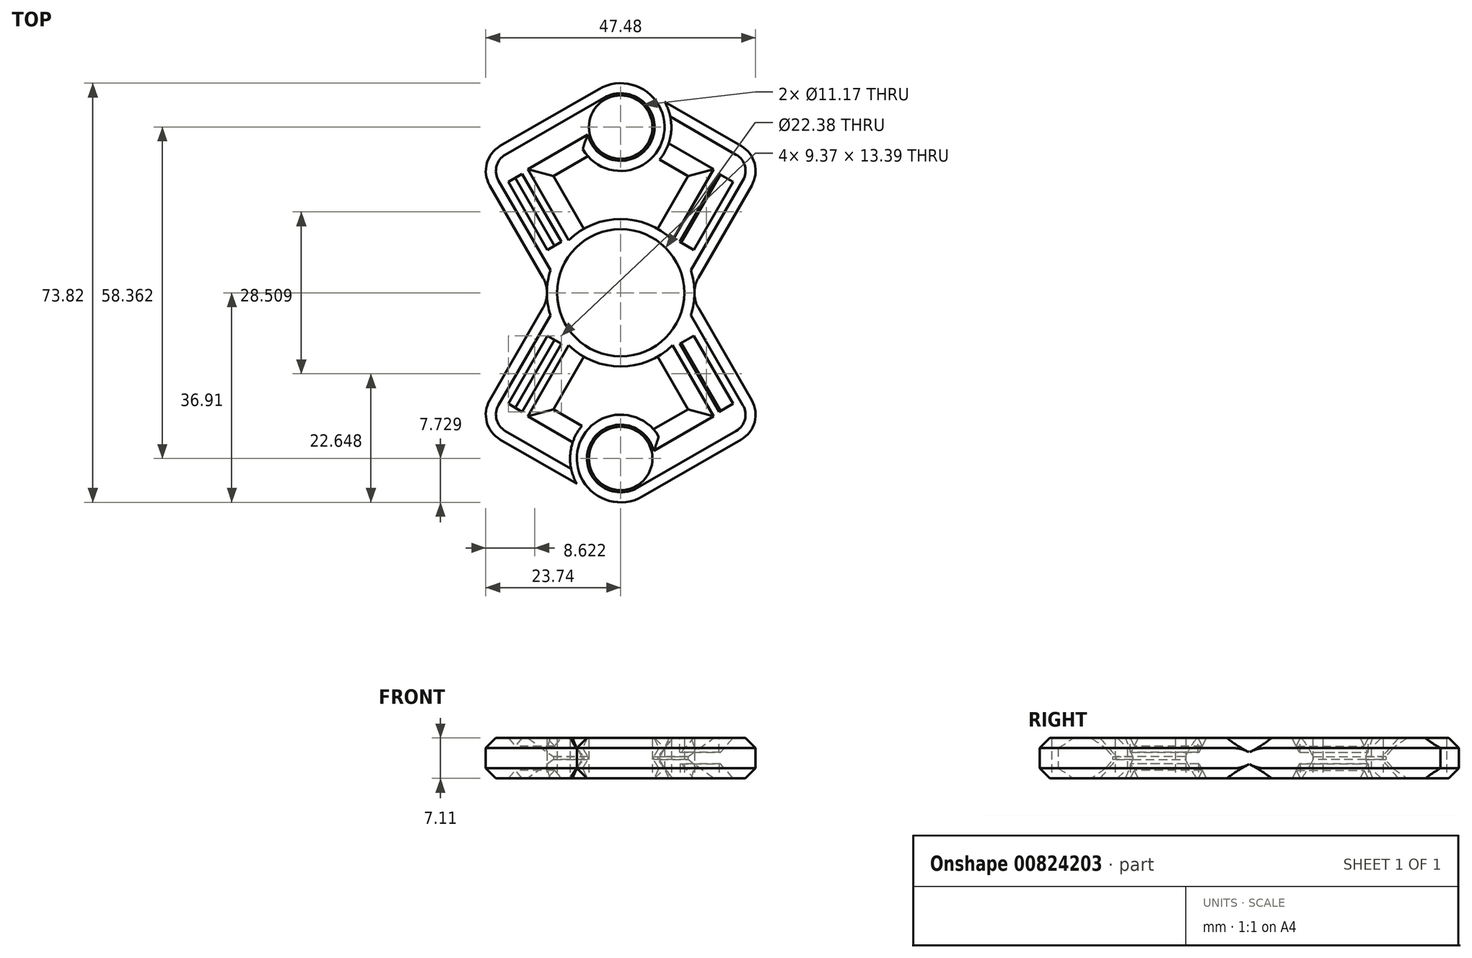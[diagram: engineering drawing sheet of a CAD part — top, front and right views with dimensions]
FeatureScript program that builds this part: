
annotation { "Feature Type Name" : "Feature", "Feature Type Description" : "" }
export const myFeature = defineFeature(function(context is Context, id is Id, definition is map)
    precondition{}
    {
        {
            var Q0;
            Q0=qCreatedBy(makeId("Top.planeOp"),FACE);
            var sketch = newSketch(context, id + "F0", { "sketchPlane" : qUnion([Q0])});
            skCircle(sketch, "E0", {"center": v(0, 0) * mm, "radius": 11.19 * mm});
            skCircle(sketch, "E1", {"center": v(0, 0) * mm, "radius": 12.99 * mm});
            skCircle(sketch, "E2.cCircle", {"center": v(0, 0) * mm, "radius": 33 * mm, "construction": true});
            skLineSegment(sketch, "E2.0", {"start": v(0, -38.1) * mm, "end": v(-33, -19.05) * mm});
            skLineSegment(sketch, "E2.1", {"start": v(-33, -19.05) * mm, "end": v(-33, 19.05) * mm});
            skLineSegment(sketch, "E2.2", {"start": v(-33, 19.05) * mm, "end": v(0, 38.1) * mm});
            skLineSegment(sketch, "E2.3", {"start": v(0, 38.1) * mm, "end": v(33, 19.05) * mm});
            skLineSegment(sketch, "E2.4", {"start": v(33, 19.05) * mm, "end": v(33, -19.05) * mm});
            skLineSegment(sketch, "E2.5", {"start": v(33, -19.05) * mm, "end": v(0, -38.1) * mm});
            skPoint(sketch, "E2.0.midPoint", {"position": v(-16.5, -28.58) * mm});
            skLineSegment(sketch, "E3", {"start": v(16.5, 28.57) * mm, "end": v(-16.5, -28.58) * mm});
            skLineSegment(sketch, "E4", {"start": v(-16.5, 28.57) * mm, "end": v(16.5, -28.57) * mm});
            skLineSegment(sketch, "E5", {"start": v(25.6, 23.32) * mm, "end": v(12.92, 1.34) * mm});
            skLineSegment(sketch, "E6.MirrorCS", {"start": v(-25.6, 23.32) * mm, "end": v(-12.92, 1.34) * mm});
            skLineSegment(sketch, "E7.MirrorCS", {"start": v(25.6, -23.32) * mm, "end": v(12.92, -1.34) * mm});
            skLineSegment(sketch, "E8.MirrorCS", {"start": v(-25.6, -23.32) * mm, "end": v(-12.92, -1.34) * mm});
            skLineSegment(sketch, "E9", {"start": v(-11.86, 20.54) * mm, "end": v(0, 27.38) * mm});
            skLineSegment(sketch, "E10.MirrorCS", {"start": v(11.86, 20.54) * mm, "end": v(0, 27.38) * mm});
            skLineSegment(sketch, "E11.MirrorCS", {"start": v(11.86, -20.54) * mm, "end": v(0, -27.38) * mm});
            skLineSegment(sketch, "E12.MirrorCS", {"start": v(-11.86, -20.54) * mm, "end": v(0, -27.38) * mm});
            skCircle(sketch, "E13", {"center": v(0, 29.18) * mm, "radius": 5.59 * mm});
            skCircle(sketch, "E14.MirrorC", {"center": v(0, -29.18) * mm, "radius": 5.59 * mm});
            skCircle(sketch, "E15", {"center": v(0, 29.18) * mm, "radius": 7.72 * mm});
            skCircle(sketch, "E16.MirrorC", {"center": v(0, -29.18) * mm, "radius": 7.72 * mm});
            skCircle(sketch, "E17", {"center": v(0, 29.18) * mm, "radius": 8.92 * mm});
            skCircle(sketch, "E18.MirrorC", {"center": v(0, -29.18) * mm, "radius": 8.92 * mm});
            skSolve(sketch);
        }
        {
            var Q0;
            {var subQ6=sQuery(id+"F0.wireOp",EDGE,"E7.MirrorCS");Q0=makeQuery(id+"F0.imprint","IMPRINT",FACE,{"disambiguationData":[TD([[makeQuery(id+"F0.imprint","IMPRINT",EDGE,{"derivedFrom":subQ6}),1.0]])]});}
            var Q1;
            {var subQ6=sQuery(id+"F0.wireOp",EDGE,"E8.MirrorCS");Q1=makeQuery(id+"F0.imprint","IMPRINT",FACE,{"disambiguationData":[TD([[makeQuery(id+"F0.imprint","IMPRINT",EDGE,{"derivedFrom":subQ6}),-1.0]])]});}
            var Q2;
            {var subQ4=sQuery(id+"F0.wireOp",EDGE,"E6.MirrorCS");Q2=makeQuery(id+"F0.imprint","IMPRINT",FACE,{"disambiguationData":[TD([[makeQuery(id+"F0.imprint","IMPRINT",EDGE,{"derivedFrom":subQ4}),1.0]])]});}
            var Q3;
            {var subQ0=sQuery(id+"F0.wireOp",EDGE,"E4");var subQ1=sQuery(id+"F0.wireOp",EDGE,"E2.2");var subQ2=makeQuery(id+"F0.imprint","INTERSECT",VERTEX,{"derivedFrom":[subQ1,subQ0]});Q3=makeQuery(id+"F0.imprint","IMPRINT",FACE,{"disambiguationData":[TD([[makeQuery(id+"F0.imprint","IMPRINT",EDGE,{"disambiguationData":[TD([[subQ2,-1.0]])],"derivedFrom":subQ1}),-1.0]])]});}
            var Q4;
            {var subQ1=sQuery(id+"F0.wireOp",EDGE,"E9");var subQ5=sQuery(id+"F0.wireOp",EDGE,"E15");var subQ9=makeQuery(id+"F0.imprint","INTERSECT",VERTEX,{"derivedFrom":[subQ1,subQ5]});Q4=makeQuery(id+"F0.imprint","IMPRINT",FACE,{"disambiguationData":[TD([[makeQuery(id+"F0.imprint","IMPRINT",EDGE,{"disambiguationData":[TD([[subQ9,-1.0]])],"derivedFrom":subQ1}),1.0]])]});}
            var Q5;
            {var subQ0=sQuery(id+"F0.wireOp",EDGE,"E15");var subQ1=sQuery(id+"F0.wireOp",EDGE,"E9");var subQ2=makeQuery(id+"F0.imprint","INTERSECT",VERTEX,{"derivedFrom":[subQ1,subQ0]});Q5=makeQuery(id+"F0.imprint","IMPRINT",FACE,{"disambiguationData":[TD([[makeQuery(id+"F0.imprint","IMPRINT",EDGE,{"disambiguationData":[TD([[subQ2,-1.0]])],"derivedFrom":subQ1}),-1.0]])]});}
            var Q6;
            {var subQ0=sQuery(id+"F0.wireOp",EDGE,"E16.MirrorC");var subQ4=sQuery(id+"F0.wireOp",EDGE,"E11.MirrorCS");var subQ9=makeQuery(id+"F0.imprint","INTERSECT",VERTEX,{"derivedFrom":[subQ4,subQ0]});Q6=makeQuery(id+"F0.imprint","IMPRINT",FACE,{"disambiguationData":[TD([[makeQuery(id+"F0.imprint","IMPRINT",EDGE,{"disambiguationData":[TD([[subQ9,-1.0]])],"derivedFrom":subQ4}),1.0]])]});}
            var Q7;
            {var subQ0=sQuery(id+"F0.wireOp",EDGE,"E16.MirrorC");var subQ1=sQuery(id+"F0.wireOp",EDGE,"E11.MirrorCS");var subQ2=makeQuery(id+"F0.imprint","INTERSECT",VERTEX,{"derivedFrom":[subQ1,subQ0]});Q7=makeQuery(id+"F0.imprint","IMPRINT",FACE,{"disambiguationData":[TD([[makeQuery(id+"F0.imprint","IMPRINT",EDGE,{"disambiguationData":[TD([[subQ2,-1.0]])],"derivedFrom":subQ1}),-1.0]])]});}
            var Q8;
            {var subQ0=sQuery(id+"F0.wireOp",EDGE,"E4");var subQ1=sQuery(id+"F0.wireOp",EDGE,"E2.5");var subQ2=makeQuery(id+"F0.imprint","INTERSECT",VERTEX,{"derivedFrom":[subQ1,subQ0]});Q8=makeQuery(id+"F0.imprint","IMPRINT",FACE,{"disambiguationData":[TD([[makeQuery(id+"F0.imprint","IMPRINT",EDGE,{"disambiguationData":[TD([[subQ2,-1.0]])],"derivedFrom":subQ1}),-1.0]])]});}
            var Q9;
            {var subQ0=sQuery(id+"F0.wireOp",EDGE,"E18.MirrorC");var subQ1=sQuery(id+"F0.wireOp",EDGE,"E2.5");var subQ2=makeQuery(id+"F0.imprint","INTERSECT",VERTEX,{"derivedFrom":[subQ1,subQ0]});Q9=makeQuery(id+"F0.imprint","IMPRINT",FACE,{"disambiguationData":[TD([[makeQuery(id+"F0.imprint","IMPRINT",EDGE,{"disambiguationData":[TD([[subQ2,-1.0]])],"derivedFrom":subQ1}),-1.0]])]});}
            var Q10;
            {var subQ0=sQuery(id+"F0.wireOp",EDGE,"E3");var subQ1=sQuery(id+"F0.wireOp",EDGE,"E2.0");var subQ2=makeQuery(id+"F0.imprint","INTERSECT",VERTEX,{"derivedFrom":[subQ1,subQ0]});Q10=makeQuery(id+"F0.imprint","IMPRINT",FACE,{"disambiguationData":[TD([[makeQuery(id+"F0.imprint","IMPRINT",EDGE,{"disambiguationData":[TD([[subQ2,1.0]])],"derivedFrom":subQ1}),-1.0]])]});}
            var Q11;
            {var subQ0=sQuery(id+"F0.wireOp",EDGE,"E17");var subQ1=sQuery(id+"F0.wireOp",EDGE,"E2.2");var subQ2=makeQuery(id+"F0.imprint","INTERSECT",VERTEX,{"derivedFrom":[subQ1,subQ0]});Q11=makeQuery(id+"F0.imprint","IMPRINT",FACE,{"disambiguationData":[TD([[makeQuery(id+"F0.imprint","IMPRINT",EDGE,{"disambiguationData":[TD([[subQ2,-1.0]])],"derivedFrom":subQ1}),-1.0]])]});}
            var Q12;
            {var subQ0=sQuery(id+"F0.wireOp",EDGE,"E3");var subQ1=sQuery(id+"F0.wireOp",EDGE,"E2.3");var subQ2=makeQuery(id+"F0.imprint","INTERSECT",VERTEX,{"derivedFrom":[subQ1,subQ0]});Q12=makeQuery(id+"F0.imprint","IMPRINT",FACE,{"disambiguationData":[TD([[makeQuery(id+"F0.imprint","IMPRINT",EDGE,{"disambiguationData":[TD([[subQ2,1.0]])],"derivedFrom":subQ1}),-1.0]])]});}
            var Q13;
            {var subQ6=sQuery(id+"F0.wireOp",EDGE,"E5");Q13=makeQuery(id+"F0.imprint","IMPRINT",FACE,{"disambiguationData":[TD([[makeQuery(id+"F0.imprint","IMPRINT",EDGE,{"derivedFrom":subQ6}),-1.0]])]});}
            extrude(context, id + "F1", {"entities" : qUnion([Q0, Q1, Q2, Q3, Q4, Q5, Q6, Q7, Q8, Q9, Q10, Q11, Q12, Q13]), "depth" : 7.11 * mm, "offsetDistance" : 25.4 * mm});
        }
        {
            var Q0;
            {var subQ0=sQuery(id+"F0.wireOp",EDGE,"E3");var subQ1=sQuery(id+"F0.wireOp",EDGE,"E0");var subQ2=makeQuery(id+"F0.imprint","INTERSECT",VERTEX,{"disambiguationData":[OD(1.0)],"derivedFrom":[subQ1,subQ0]});Q0=makeQuery(id+"F0.imprint","IMPRINT",FACE,{"disambiguationData":[TD([[makeQuery(id+"F0.imprint","IMPRINT",EDGE,{"disambiguationData":[TD([[subQ2,-1.0]])],"derivedFrom":subQ1}),-1.0]])]});}
            var Q1;
            {var subQ5=sQuery(id+"F0.wireOp",EDGE,"E4");var subQ7=sQuery(id+"F0.wireOp",EDGE,"E0");var subQ9=makeQuery(id+"F0.imprint","INTERSECT",VERTEX,{"disambiguationData":[OD(0.0)],"derivedFrom":[subQ7,subQ5]});Q1=makeQuery(id+"F0.imprint","IMPRINT",FACE,{"disambiguationData":[TD([[makeQuery(id+"F0.imprint","IMPRINT",EDGE,{"disambiguationData":[TD([[subQ9,-1.0]])],"derivedFrom":subQ7}),-1.0]])]});}
            var Q2;
            {var subQ0=sQuery(id+"F0.wireOp",EDGE,"E4");var subQ1=sQuery(id+"F0.wireOp",EDGE,"E0");var subQ2=makeQuery(id+"F0.imprint","INTERSECT",VERTEX,{"disambiguationData":[OD(0.0)],"derivedFrom":[subQ1,subQ0]});Q2=makeQuery(id+"F0.imprint","IMPRINT",FACE,{"disambiguationData":[TD([[makeQuery(id+"F0.imprint","IMPRINT",EDGE,{"disambiguationData":[TD([[subQ2,1.0]])],"derivedFrom":subQ1}),-1.0]])]});}
            var Q3;
            {var subQ5=sQuery(id+"F0.wireOp",EDGE,"E3");var subQ7=sQuery(id+"F0.wireOp",EDGE,"E0");var subQ8=makeQuery(id+"F0.imprint","INTERSECT",VERTEX,{"disambiguationData":[OD(0.0)],"derivedFrom":[subQ7,subQ5]});Q3=makeQuery(id+"F0.imprint","IMPRINT",FACE,{"disambiguationData":[TD([[makeQuery(id+"F0.imprint","IMPRINT",EDGE,{"disambiguationData":[TD([[subQ8,1.0]])],"derivedFrom":subQ7}),-1.0]])]});}
            extrude(context, id + "F2", {"entities" : qUnion([Q0, Q1, Q2, Q3]), "depth" : 7.11 * mm, "offsetDistance" : 25.4 * mm});
        }
        {
            var Q0;
            Q0=makeQuery(id+"F1.opExtrude","SWEPT_EDGE",EDGE,{"disambiguationData":[OSD([sQuery(id+"F0.wireOp",EDGE,"E2.5"),sQuery(id+"F0.wireOp",EDGE,"E7.MirrorCS")])]});
            var Q1;
            Q1=makeQuery(id+"F1.opExtrude","SWEPT_EDGE",EDGE,{"disambiguationData":[OSD([sQuery(id+"F0.wireOp",EDGE,"E2.3"),sQuery(id+"F0.wireOp",EDGE,"E5")])]});
            var Q2;
            Q2=makeQuery(id+"F1.opExtrude","SWEPT_EDGE",EDGE,{"disambiguationData":[OSD([sQuery(id+"F0.wireOp",EDGE,"E2.2"),sQuery(id+"F0.wireOp",EDGE,"E6.MirrorCS")])]});
            var Q3;
            Q3=makeQuery(id+"F1.opExtrude","SWEPT_EDGE",EDGE,{"disambiguationData":[OSD([sQuery(id+"F0.wireOp",EDGE,"E2.0"),sQuery(id+"F0.wireOp",EDGE,"E8.MirrorCS")])]});
            fillet(context, id + "F3", {"entities" : qUnion([Q0, Q1, Q2, Q3]), "radius" : 5.08 * mm, "tangentPropagation" : true, "allowEdgeOverflow" : false});
        }
        {
            var Q0;
            Q0=makeQuery(id+"F1.opExtrude","CAP_EDGE",EDGE,{"disambiguationData":[OSD([sQuery(id+"F0.wireOp",EDGE,"E7.MirrorCS")])],"isStart":true});
            var Q1;
            Q1=makeQuery(id+"F1.opExtrude","CAP_EDGE",EDGE,{"disambiguationData":[OSD([sQuery(id+"F0.wireOp",EDGE,"E2.5")])],"isStart":true});
            var Q2;
            Q2=makeQuery(id+"F1.opExtrude","CAP_EDGE",EDGE,{"disambiguationData":[OSD([sQuery(id+"F0.wireOp",EDGE,"E5")])],"isStart":true});
            var Q3;
            {var subQ0=sQuery(id+"F0.wireOp",EDGE,"E2.3");var subQ1=makeQuery(id+"F0.imprint","INTERSECT",VERTEX,{"derivedFrom":[subQ0,sQuery(id+"F0.wireOp",EDGE,"E3")]});Q3=makeQuery(id+"F1.opExtrude","CAP_EDGE",EDGE,{"disambiguationData":[OSD([subQ0]),TDD([makeQuery(id+"F0.imprint","IMPRINT",EDGE,{"disambiguationData":[TD([[subQ1,1.0]])],"derivedFrom":subQ0}),makeQuery(id+"F0.imprint","IMPRINT",EDGE,{"disambiguationData":[TD([[subQ1,-1.0]])],"derivedFrom":subQ0})])],"isStart":true});}
            var Q4;
            Q4=makeQuery(id+"F1.opExtrude","CAP_EDGE",EDGE,{"disambiguationData":[OSD([sQuery(id+"F0.wireOp",EDGE,"E2.2")])],"isStart":true});
            var Q5;
            Q5=makeQuery(id+"F1.opExtrude","CAP_EDGE",EDGE,{"disambiguationData":[OSD([sQuery(id+"F0.wireOp",EDGE,"E6.MirrorCS")])],"isStart":true});
            var Q6;
            Q6=makeQuery(id+"F1.opExtrude","CAP_EDGE",EDGE,{"disambiguationData":[OSD([sQuery(id+"F0.wireOp",EDGE,"E8.MirrorCS")])],"isStart":true});
            var Q7;
            {var subQ0=sQuery(id+"F0.wireOp",EDGE,"E2.0");var subQ1=makeQuery(id+"F0.imprint","INTERSECT",VERTEX,{"derivedFrom":[subQ0,sQuery(id+"F0.wireOp",EDGE,"E3")]});Q7=makeQuery(id+"F1.opExtrude","CAP_EDGE",EDGE,{"disambiguationData":[OSD([subQ0]),TDD([makeQuery(id+"F0.imprint","IMPRINT",EDGE,{"disambiguationData":[TD([[subQ1,1.0]])],"derivedFrom":subQ0}),makeQuery(id+"F0.imprint","IMPRINT",EDGE,{"disambiguationData":[TD([[subQ1,-1.0]])],"derivedFrom":subQ0})])],"isStart":true});}
            var Q8;
            Q8=makeQuery(id+"F1.opExtrude","CAP_EDGE",EDGE,{"disambiguationData":[OSD([sQuery(id+"F0.wireOp",EDGE,"E16.MirrorC")])],"isStart":true});
            var Q9;
            Q9=makeQuery(id+"F1.opExtrude","CAP_EDGE",EDGE,{"disambiguationData":[OSD([sQuery(id+"F0.wireOp",EDGE,"E15")])],"isStart":true});
            var Q10;
            Q10=makeQuery(id+"F1.opExtrude","CAP_EDGE",EDGE,{"disambiguationData":[OSD([sQuery(id+"F0.wireOp",EDGE,"E15")])],"isStart":false});
            var Q11;
            Q11=makeQuery(id+"F1.opExtrude","CAP_EDGE",EDGE,{"disambiguationData":[OSD([sQuery(id+"F0.wireOp",EDGE,"E2.2")])],"isStart":false});
            var Q12;
            Q12=makeQuery(id+"F1.opExtrude","CAP_EDGE",EDGE,{"disambiguationData":[OSD([sQuery(id+"F0.wireOp",EDGE,"E6.MirrorCS")])],"isStart":false});
            var Q13;
            Q13=makeQuery(id+"F1.opExtrude","CAP_EDGE",EDGE,{"disambiguationData":[OSD([sQuery(id+"F0.wireOp",EDGE,"E8.MirrorCS")])],"isStart":false});
            var Q14;
            {var subQ0=sQuery(id+"F0.wireOp",EDGE,"E2.0");var subQ1=makeQuery(id+"F0.imprint","INTERSECT",VERTEX,{"derivedFrom":[subQ0,sQuery(id+"F0.wireOp",EDGE,"E3")]});Q14=makeQuery(id+"F1.opExtrude","CAP_EDGE",EDGE,{"disambiguationData":[OSD([subQ0]),TDD([makeQuery(id+"F0.imprint","IMPRINT",EDGE,{"disambiguationData":[TD([[subQ1,1.0]])],"derivedFrom":subQ0}),makeQuery(id+"F0.imprint","IMPRINT",EDGE,{"disambiguationData":[TD([[subQ1,-1.0]])],"derivedFrom":subQ0})])],"isStart":false});}
            var Q15;
            Q15=makeQuery(id+"F1.opExtrude","CAP_EDGE",EDGE,{"disambiguationData":[OSD([sQuery(id+"F0.wireOp",EDGE,"E16.MirrorC")])],"isStart":false});
            var Q16;
            Q16=makeQuery(id+"F1.opExtrude","CAP_EDGE",EDGE,{"disambiguationData":[OSD([sQuery(id+"F0.wireOp",EDGE,"E2.5")])],"isStart":false});
            var Q17;
            Q17=makeQuery(id+"F1.opExtrude","CAP_EDGE",EDGE,{"disambiguationData":[OSD([sQuery(id+"F0.wireOp",EDGE,"E7.MirrorCS")])],"isStart":false});
            var Q18;
            Q18=makeQuery(id+"F1.opExtrude","CAP_EDGE",EDGE,{"disambiguationData":[OSD([sQuery(id+"F0.wireOp",EDGE,"E5")])],"isStart":false});
            var Q19;
            {var subQ0=sQuery(id+"F0.wireOp",EDGE,"E2.3");var subQ1=makeQuery(id+"F0.imprint","INTERSECT",VERTEX,{"derivedFrom":[subQ0,sQuery(id+"F0.wireOp",EDGE,"E3")]});Q19=makeQuery(id+"F1.opExtrude","CAP_EDGE",EDGE,{"disambiguationData":[OSD([subQ0]),TDD([makeQuery(id+"F0.imprint","IMPRINT",EDGE,{"disambiguationData":[TD([[subQ1,1.0]])],"derivedFrom":subQ0}),makeQuery(id+"F0.imprint","IMPRINT",EDGE,{"disambiguationData":[TD([[subQ1,-1.0]])],"derivedFrom":subQ0})])],"isStart":false});}
            chamfer(context, id + "F4", {"entities" : qUnion([Q0, Q1, Q2, Q3, Q4, Q5, Q6, Q7, Q8, Q9, Q10, Q11, Q12, Q13, Q14, Q15, Q16, Q17, Q18, Q19]), "width" : 1.78 * mm, "tangentPropagation" : true});
        }
        {
            var Q0;
            Q0=makeQuery(id+"F1.opExtrude","CAP_EDGE",EDGE,{"disambiguationData":[OSD([sQuery(id+"F0.wireOp",EDGE,"E11.MirrorCS")])],"isStart":true});
            var Q1;
            {var subQ0=sQuery(id+"F0.wireOp",EDGE,"E4");Q1=makeQuery(id+"F1.opExtrude","CAP_EDGE",EDGE,{"disambiguationData":[OSD([subQ0]),TDD([makeQuery(id+"F0.imprint","IMPRINT",EDGE,{"disambiguationData":[TD([[makeQuery(id+"F0.imprint","INTERSECT",VERTEX,{"derivedFrom":[subQ0,sQuery(id+"F0.wireOp",EDGE,"E11.MirrorCS")]}),1.0]])],"derivedFrom":subQ0})])],"isStart":true});}
            var Q2;
            Q2=makeQuery(id+"F1.opExtrude","CAP_EDGE",EDGE,{"disambiguationData":[OSD([sQuery(id+"F0.wireOp",EDGE,"E12.MirrorCS")])],"isStart":true});
            var Q3;
            {var subQ0=sQuery(id+"F0.wireOp",EDGE,"E3");Q3=makeQuery(id+"F1.opExtrude","CAP_EDGE",EDGE,{"disambiguationData":[OSD([subQ0]),TDD([makeQuery(id+"F0.imprint","IMPRINT",EDGE,{"disambiguationData":[TD([[makeQuery(id+"F0.imprint","INTERSECT",VERTEX,{"derivedFrom":[subQ0,sQuery(id+"F0.wireOp",EDGE,"E12.MirrorCS")]}),1.0]])],"derivedFrom":subQ0})])],"isStart":true});}
            var Q4;
            {var subQ0=sQuery(id+"F0.wireOp",EDGE,"E4");Q4=makeQuery(id+"F1.opExtrude","CAP_EDGE",EDGE,{"disambiguationData":[OSD([subQ0]),TDD([makeQuery(id+"F0.imprint","IMPRINT",EDGE,{"disambiguationData":[TD([[makeQuery(id+"F0.imprint","INTERSECT",VERTEX,{"derivedFrom":[subQ0,sQuery(id+"F0.wireOp",EDGE,"E11.MirrorCS")]}),1.0]])],"derivedFrom":subQ0})])],"isStart":false});}
            var Q5;
            Q5=makeQuery(id+"F1.opExtrude","CAP_EDGE",EDGE,{"disambiguationData":[OSD([sQuery(id+"F0.wireOp",EDGE,"E11.MirrorCS")])],"isStart":false});
            var Q6;
            Q6=makeQuery(id+"F1.opExtrude","CAP_EDGE",EDGE,{"disambiguationData":[OSD([sQuery(id+"F0.wireOp",EDGE,"E12.MirrorCS")])],"isStart":false});
            var Q7;
            {var subQ0=sQuery(id+"F0.wireOp",EDGE,"E3");Q7=makeQuery(id+"F1.opExtrude","CAP_EDGE",EDGE,{"disambiguationData":[OSD([subQ0]),TDD([makeQuery(id+"F0.imprint","IMPRINT",EDGE,{"disambiguationData":[TD([[makeQuery(id+"F0.imprint","INTERSECT",VERTEX,{"derivedFrom":[subQ0,sQuery(id+"F0.wireOp",EDGE,"E12.MirrorCS")]}),1.0]])],"derivedFrom":subQ0})])],"isStart":false});}
            var Q8;
            {var subQ0=sQuery(id+"F0.wireOp",EDGE,"E4");Q8=makeQuery(id+"F1.opExtrude","CAP_EDGE",EDGE,{"disambiguationData":[OSD([subQ0]),TDD([makeQuery(id+"F0.imprint","IMPRINT",EDGE,{"disambiguationData":[TD([[makeQuery(id+"F0.imprint","INTERSECT",VERTEX,{"derivedFrom":[subQ0,sQuery(id+"F0.wireOp",EDGE,"E9")]}),-1.0]])],"derivedFrom":subQ0})])],"isStart":true});}
            var Q9;
            Q9=makeQuery(id+"F1.opExtrude","CAP_EDGE",EDGE,{"disambiguationData":[OSD([sQuery(id+"F0.wireOp",EDGE,"E9")])],"isStart":true});
            var Q10;
            {var subQ0=sQuery(id+"F0.wireOp",EDGE,"E3");Q10=makeQuery(id+"F1.opExtrude","CAP_EDGE",EDGE,{"disambiguationData":[OSD([subQ0]),TDD([makeQuery(id+"F0.imprint","IMPRINT",EDGE,{"disambiguationData":[TD([[makeQuery(id+"F0.imprint","INTERSECT",VERTEX,{"derivedFrom":[subQ0,sQuery(id+"F0.wireOp",EDGE,"E10.MirrorCS")]}),-1.0]])],"derivedFrom":subQ0})])],"isStart":true});}
            var Q11;
            Q11=makeQuery(id+"F1.opExtrude","CAP_EDGE",EDGE,{"disambiguationData":[OSD([sQuery(id+"F0.wireOp",EDGE,"E10.MirrorCS")])],"isStart":true});
            var Q12;
            {var subQ0=sQuery(id+"F0.wireOp",EDGE,"E3");Q12=makeQuery(id+"F1.opExtrude","CAP_EDGE",EDGE,{"disambiguationData":[OSD([subQ0]),TDD([makeQuery(id+"F0.imprint","IMPRINT",EDGE,{"disambiguationData":[TD([[makeQuery(id+"F0.imprint","INTERSECT",VERTEX,{"derivedFrom":[subQ0,sQuery(id+"F0.wireOp",EDGE,"E10.MirrorCS")]}),-1.0]])],"derivedFrom":subQ0})])],"isStart":false});}
            var Q13;
            Q13=makeQuery(id+"F1.opExtrude","CAP_EDGE",EDGE,{"disambiguationData":[OSD([sQuery(id+"F0.wireOp",EDGE,"E10.MirrorCS")])],"isStart":false});
            var Q14;
            {var subQ0=sQuery(id+"F0.wireOp",EDGE,"E4");Q14=makeQuery(id+"F1.opExtrude","CAP_EDGE",EDGE,{"disambiguationData":[OSD([subQ0]),TDD([makeQuery(id+"F0.imprint","IMPRINT",EDGE,{"disambiguationData":[TD([[makeQuery(id+"F0.imprint","INTERSECT",VERTEX,{"derivedFrom":[subQ0,sQuery(id+"F0.wireOp",EDGE,"E9")]}),-1.0]])],"derivedFrom":subQ0})])],"isStart":false});}
            var Q15;
            Q15=makeQuery(id+"F1.opExtrude","CAP_EDGE",EDGE,{"disambiguationData":[OSD([sQuery(id+"F0.wireOp",EDGE,"E9")])],"isStart":false});
            chamfer(context, id + "F5", {"entities" : qUnion([Q0, Q1, Q2, Q3, Q4, Q5, Q6, Q7, Q8, Q9, Q10, Q11, Q12, Q13, Q14, Q15]), "width" : 3.3 * mm, "tangentPropagation" : true});
        }
        {
            var Q0;
            Q0=makeQuery(id+"F1.opExtrude","SWEPT_BODY",BODY,{"disambiguationData":[OSD([sQuery(id+"F0.wireOp",EDGE,"E1"),sQuery(id+"F0.wireOp",EDGE,"E2.3"),sQuery(id+"F0.wireOp",EDGE,"E3"),sQuery(id+"F0.wireOp",EDGE,"E5"),sQuery(id+"F0.wireOp",EDGE,"E10.MirrorCS"),sQuery(id+"F0.wireOp",EDGE,"E17")])]});
            var Q1;
            Q1=makeQuery(id+"F1.opExtrude","SWEPT_BODY",BODY,{"disambiguationData":[OSD([sQuery(id+"F0.wireOp",EDGE,"E1"),sQuery(id+"F0.wireOp",EDGE,"E2.2"),sQuery(id+"F0.wireOp",EDGE,"E4"),sQuery(id+"F0.wireOp",EDGE,"E6.MirrorCS"),sQuery(id+"F0.wireOp",EDGE,"E9"),sQuery(id+"F0.wireOp",EDGE,"E13"),sQuery(id+"F0.wireOp",EDGE,"E15")])]});
            var Q2;
            Q2=makeQuery(id+"F1.opExtrude","SWEPT_BODY",BODY,{"disambiguationData":[OSD([sQuery(id+"F0.wireOp",EDGE,"E1"),sQuery(id+"F0.wireOp",EDGE,"E2.0"),sQuery(id+"F0.wireOp",EDGE,"E3"),sQuery(id+"F0.wireOp",EDGE,"E8.MirrorCS"),sQuery(id+"F0.wireOp",EDGE,"E12.MirrorCS"),sQuery(id+"F0.wireOp",EDGE,"E18.MirrorC")])]});
            var Q3;
            Q3=makeQuery(id+"F1.opExtrude","SWEPT_BODY",BODY,{"disambiguationData":[OSD([sQuery(id+"F0.wireOp",EDGE,"E1"),sQuery(id+"F0.wireOp",EDGE,"E2.5"),sQuery(id+"F0.wireOp",EDGE,"E4"),sQuery(id+"F0.wireOp",EDGE,"E7.MirrorCS"),sQuery(id+"F0.wireOp",EDGE,"E11.MirrorCS"),sQuery(id+"F0.wireOp",EDGE,"E14.MirrorC"),sQuery(id+"F0.wireOp",EDGE,"E16.MirrorC")])]});
            var Q4;
            Q4=makeQuery(id+"F2.opExtrude","SWEPT_BODY",BODY,{"disambiguationData":[OSD([sQuery(id+"F0.wireOp",EDGE,"E0"),sQuery(id+"F0.wireOp",EDGE,"E1")])]});
            booleanBodies(context, id + "F6", {"operationType" : BooleanOperationType.UNION, "tools" : qUnion([Q0, Q1, Q2, Q3, Q4])});
        }
        {
            var Q0;
            Q0=makeQuery(id+"F1.opExtrude","SWEPT_EDGE",EDGE,{"disambiguationData":[OSD([sQuery(id+"F0.wireOp",EDGE,"E1"),sQuery(id+"F0.wireOp",EDGE,"E8.MirrorCS")])]});
            var Q1;
            Q1=makeQuery(id+"F1.opExtrude","SWEPT_EDGE",EDGE,{"disambiguationData":[OSD([sQuery(id+"F0.wireOp",EDGE,"E1"),sQuery(id+"F0.wireOp",EDGE,"E6.MirrorCS")])]});
            var Q2;
            Q2=makeQuery(id+"F1.opExtrude","SWEPT_EDGE",EDGE,{"disambiguationData":[OSD([sQuery(id+"F0.wireOp",EDGE,"E1"),sQuery(id+"F0.wireOp",EDGE,"E7.MirrorCS")])]});
            var Q3;
            Q3=makeQuery(id+"F1.opExtrude","SWEPT_EDGE",EDGE,{"disambiguationData":[OSD([sQuery(id+"F0.wireOp",EDGE,"E1"),sQuery(id+"F0.wireOp",EDGE,"E5")])]});
            fillet(context, id + "F7", {"entities" : qUnion([Q0, Q1, Q2, Q3]), "radius" : 5.08 * mm, "tangentPropagation" : true, "allowEdgeOverflow" : false});
        }
        {
            var Q0;
            {var subQ0=sQuery(id+"F0.wireOp",EDGE,"E4");var subQ1=sQuery(id+"F0.wireOp",EDGE,"E1");var subQ2=sQuery(id+"F0.wireOp",EDGE,"E3");Q0=makeQuery(id+"F6.opBoolean","MERGE",FACE,{"derivedFrom":[makeQuery(id+"F2.opExtrude","CAP_FACE",FACE,{"disambiguationData":[OSD([sQuery(id+"F0.wireOp",EDGE,"E0"),subQ1])],"isStart":true}),makeQuery(id+"F1.opExtrude","CAP_FACE",FACE,{"disambiguationData":[OSD([subQ1,sQuery(id+"F0.wireOp",EDGE,"E2.3"),subQ2,sQuery(id+"F0.wireOp",EDGE,"E5"),sQuery(id+"F0.wireOp",EDGE,"E10.MirrorCS"),sQuery(id+"F0.wireOp",EDGE,"E17")])],"isStart":true}),makeQuery(id+"F1.opExtrude","CAP_FACE",FACE,{"disambiguationData":[OSD([subQ1,sQuery(id+"F0.wireOp",EDGE,"E2.2"),subQ0,sQuery(id+"F0.wireOp",EDGE,"E6.MirrorCS"),sQuery(id+"F0.wireOp",EDGE,"E9"),sQuery(id+"F0.wireOp",EDGE,"E13"),sQuery(id+"F0.wireOp",EDGE,"E15")])],"isStart":true}),makeQuery(id+"F1.opExtrude","CAP_FACE",FACE,{"disambiguationData":[OSD([subQ1,sQuery(id+"F0.wireOp",EDGE,"E2.0"),subQ2,sQuery(id+"F0.wireOp",EDGE,"E8.MirrorCS"),sQuery(id+"F0.wireOp",EDGE,"E12.MirrorCS"),sQuery(id+"F0.wireOp",EDGE,"E18.MirrorC")])],"isStart":true}),makeQuery(id+"F1.opExtrude","CAP_FACE",FACE,{"disambiguationData":[OSD([subQ1,sQuery(id+"F0.wireOp",EDGE,"E2.5"),subQ0,sQuery(id+"F0.wireOp",EDGE,"E7.MirrorCS"),sQuery(id+"F0.wireOp",EDGE,"E11.MirrorCS"),sQuery(id+"F0.wireOp",EDGE,"E14.MirrorC"),sQuery(id+"F0.wireOp",EDGE,"E16.MirrorC")])],"isStart":true})]});}
            var sketch = newSketch(context, id + "F8", { "sketchPlane" : qUnion([Q0])});
            skLineSegment(sketch, "E19", {"start": v(10.43, 8.97) * mm, "end": v(17.34, 20.95) * mm});
            skLineSegment(sketch, "E20", {"start": v(17.34, 20.95) * mm, "end": v(19.8, 19.53) * mm});
            skLineSegment(sketch, "E21.MirrorCS", {"start": v(10.43, 8.97) * mm, "end": v(12.88, 7.56) * mm});
            skLineSegment(sketch, "E22.MirrorCS", {"start": v(17.34, 20.95) * mm, "end": v(10.43, 8.97) * mm});
            skLineSegment(sketch, "E23.MirrorCS", {"start": v(19.8, 19.53) * mm, "end": v(12.88, 7.56) * mm});
            skLineSegment(sketch, "E24.MirrorCS", {"start": v(-17.34, 20.95) * mm, "end": v(-19.8, 19.53) * mm});
            skLineSegment(sketch, "E25.MirrorCS", {"start": v(-19.8, 19.53) * mm, "end": v(-12.88, 7.56) * mm});
            skLineSegment(sketch, "E26.MirrorCS", {"start": v(-10.43, 8.97) * mm, "end": v(-12.88, 7.56) * mm});
            skLineSegment(sketch, "E27.MirrorCS", {"start": v(-17.34, 20.95) * mm, "end": v(-10.43, 8.97) * mm});
            skLineSegment(sketch, "E28.MirrorCS", {"start": v(-17.34, -20.95) * mm, "end": v(-19.8, -19.53) * mm});
            skLineSegment(sketch, "E29.MirrorCS", {"start": v(17.34, -20.95) * mm, "end": v(19.8, -19.53) * mm});
            skLineSegment(sketch, "E30.MirrorCS", {"start": v(10.43, -8.97) * mm, "end": v(12.88, -7.56) * mm});
            skLineSegment(sketch, "E31.MirrorCS", {"start": v(-10.43, -8.97) * mm, "end": v(-12.88, -7.56) * mm});
            skLineSegment(sketch, "E32.MirrorCS", {"start": v(10.43, -8.97) * mm, "end": v(17.34, -20.95) * mm});
            skLineSegment(sketch, "E33.MirrorCS", {"start": v(-19.8, -19.53) * mm, "end": v(-12.88, -7.56) * mm});
            skLineSegment(sketch, "E34.MirrorCS", {"start": v(-17.34, -20.95) * mm, "end": v(-10.43, -8.97) * mm});
            skLineSegment(sketch, "E35.MirrorCS", {"start": v(17.34, -20.95) * mm, "end": v(10.43, -8.97) * mm});
            skLineSegment(sketch, "E36.MirrorCS", {"start": v(19.8, -19.53) * mm, "end": v(12.88, -7.56) * mm});
            skSolve(sketch);
        }
        {
            var Q0;
            Q0=makeQuery(id+"F8.imprint","IMPRINT",FACE,{"disambiguationData":[TD([[makeQuery(id+"F8.imprint","IMPRINT",EDGE,{"derivedFrom":sQuery(id+"F8.wireOp",EDGE,"E24.MirrorCS")}),1.0]])]});
            var Q1;
            Q1=makeQuery(id+"F8.imprint","IMPRINT",FACE,{"disambiguationData":[TD([[makeQuery(id+"F8.imprint","IMPRINT",EDGE,{"derivedFrom":sQuery(id+"F8.wireOp",EDGE,"E28.MirrorCS")}),-1.0]])]});
            var Q2;
            Q2=makeQuery(id+"F8.imprint","IMPRINT",FACE,{"disambiguationData":[TD([[makeQuery(id+"F8.imprint","IMPRINT",EDGE,{"derivedFrom":sQuery(id+"F8.wireOp",EDGE,"E29.MirrorCS")}),1.0]])]});
            var Q3;
            Q3=makeQuery(id+"F8.imprint","IMPRINT",FACE,{"disambiguationData":[TD([[makeQuery(id+"F8.imprint","IMPRINT",EDGE,{"derivedFrom":sQuery(id+"F8.wireOp",EDGE,"E20")}),-1.0]])]});
            extrude(context, id + "F9", {"entities" : qUnion([Q0, Q1, Q2, Q3]), "operationType" : NewBodyOperationType.REMOVE, "oppositeDirection" : true, "depth" : 2.54 * mm, "offsetDistance" : 25.4 * mm});
        }
        {
            var Q0;
            Q0=makeQuery(id+"F9.boolean.opBoolean","COPY",EDGE,{"derivedFrom":makeQuery(id+"F9.opExtrude","CAP_EDGE",EDGE,{"disambiguationData":[OSD([sQuery(id+"F8.wireOp",EDGE,"E23.MirrorCS")])],"isStart":false})});
            var Q1;
            Q1=makeQuery(id+"F9.boolean.opBoolean","COPY",EDGE,{"derivedFrom":makeQuery(id+"F9.opExtrude","CAP_EDGE",EDGE,{"disambiguationData":[OSD([sQuery(id+"F8.wireOp",EDGE,"E22.MirrorCS")])],"isStart":false})});
            var Q2;
            Q2=makeQuery(id+"F9.boolean.opBoolean","COPY",EDGE,{"derivedFrom":makeQuery(id+"F9.opExtrude","CAP_EDGE",EDGE,{"disambiguationData":[OSD([sQuery(id+"F8.wireOp",EDGE,"E27.MirrorCS")])],"isStart":false})});
            var Q3;
            Q3=makeQuery(id+"F9.boolean.opBoolean","COPY",EDGE,{"derivedFrom":makeQuery(id+"F9.opExtrude","CAP_EDGE",EDGE,{"disambiguationData":[OSD([sQuery(id+"F8.wireOp",EDGE,"E25.MirrorCS")])],"isStart":false})});
            var Q4;
            Q4=makeQuery(id+"F9.boolean.opBoolean","COPY",EDGE,{"derivedFrom":makeQuery(id+"F9.opExtrude","CAP_EDGE",EDGE,{"disambiguationData":[OSD([sQuery(id+"F8.wireOp",EDGE,"E35.MirrorCS")])],"isStart":false})});
            var Q5;
            Q5=makeQuery(id+"F9.boolean.opBoolean","COPY",EDGE,{"derivedFrom":makeQuery(id+"F9.opExtrude","CAP_EDGE",EDGE,{"disambiguationData":[OSD([sQuery(id+"F8.wireOp",EDGE,"E36.MirrorCS")])],"isStart":false})});
            var Q6;
            Q6=makeQuery(id+"F9.boolean.opBoolean","COPY",EDGE,{"derivedFrom":makeQuery(id+"F9.opExtrude","CAP_EDGE",EDGE,{"disambiguationData":[OSD([sQuery(id+"F8.wireOp",EDGE,"E33.MirrorCS")])],"isStart":false})});
            var Q7;
            Q7=makeQuery(id+"F9.boolean.opBoolean","COPY",EDGE,{"derivedFrom":makeQuery(id+"F9.opExtrude","CAP_EDGE",EDGE,{"disambiguationData":[OSD([sQuery(id+"F8.wireOp",EDGE,"E34.MirrorCS")])],"isStart":false})});
            chamfer(context, id + "F10", {"entities" : qUnion([Q0, Q1, Q2, Q3, Q4, Q5, Q6, Q7]), "width" : 2.54 * mm, "tangentPropagation" : true});
        }
        {
            var Q0;
            {var subQ0=sQuery(id+"F0.wireOp",EDGE,"E4");var subQ1=sQuery(id+"F0.wireOp",EDGE,"E1");var subQ2=sQuery(id+"F0.wireOp",EDGE,"E3");Q0=makeQuery(id+"F6.opBoolean","MERGE",FACE,{"derivedFrom":[makeQuery(id+"F2.opExtrude","CAP_FACE",FACE,{"disambiguationData":[OSD([sQuery(id+"F0.wireOp",EDGE,"E0"),subQ1])],"isStart":false}),makeQuery(id+"F1.opExtrude","CAP_FACE",FACE,{"disambiguationData":[OSD([subQ1,sQuery(id+"F0.wireOp",EDGE,"E2.3"),subQ2,sQuery(id+"F0.wireOp",EDGE,"E5"),sQuery(id+"F0.wireOp",EDGE,"E10.MirrorCS"),sQuery(id+"F0.wireOp",EDGE,"E17")])],"isStart":false}),makeQuery(id+"F1.opExtrude","CAP_FACE",FACE,{"disambiguationData":[OSD([subQ1,sQuery(id+"F0.wireOp",EDGE,"E2.2"),subQ0,sQuery(id+"F0.wireOp",EDGE,"E6.MirrorCS"),sQuery(id+"F0.wireOp",EDGE,"E9"),sQuery(id+"F0.wireOp",EDGE,"E13"),sQuery(id+"F0.wireOp",EDGE,"E15")])],"isStart":false}),makeQuery(id+"F1.opExtrude","CAP_FACE",FACE,{"disambiguationData":[OSD([subQ1,sQuery(id+"F0.wireOp",EDGE,"E2.0"),subQ2,sQuery(id+"F0.wireOp",EDGE,"E8.MirrorCS"),sQuery(id+"F0.wireOp",EDGE,"E12.MirrorCS"),sQuery(id+"F0.wireOp",EDGE,"E18.MirrorC")])],"isStart":false}),makeQuery(id+"F1.opExtrude","CAP_FACE",FACE,{"disambiguationData":[OSD([subQ1,sQuery(id+"F0.wireOp",EDGE,"E2.5"),subQ0,sQuery(id+"F0.wireOp",EDGE,"E7.MirrorCS"),sQuery(id+"F0.wireOp",EDGE,"E11.MirrorCS"),sQuery(id+"F0.wireOp",EDGE,"E14.MirrorC"),sQuery(id+"F0.wireOp",EDGE,"E16.MirrorC")])],"isStart":false})]});}
            var sketch = newSketch(context, id + "F11", { "sketchPlane" : qUnion([Q0])});
            skLineSegment(sketch, "E37", {"start": v(10.42, 8.97) * mm, "end": v(17.33, 20.94) * mm});
            skLineSegment(sketch, "E38", {"start": v(17.33, 20.94) * mm, "end": v(19.78, 19.53) * mm});
            skLineSegment(sketch, "E39.MirrorCS", {"start": v(10.42, 8.97) * mm, "end": v(12.87, 7.55) * mm});
            skLineSegment(sketch, "E40.MirrorCS", {"start": v(17.33, 20.94) * mm, "end": v(10.42, 8.97) * mm});
            skLineSegment(sketch, "E41.MirrorCS", {"start": v(19.78, 19.53) * mm, "end": v(12.87, 7.55) * mm});
            skLineSegment(sketch, "E42.MirrorCS", {"start": v(-17.35, 20.94) * mm, "end": v(-19.8, 19.53) * mm});
            skLineSegment(sketch, "E43.MirrorCS", {"start": v(-19.8, 19.53) * mm, "end": v(-12.89, 7.55) * mm});
            skLineSegment(sketch, "E44.MirrorCS", {"start": v(-10.43, 8.97) * mm, "end": v(-12.89, 7.55) * mm});
            skLineSegment(sketch, "E45.MirrorCS", {"start": v(-17.35, 20.94) * mm, "end": v(-10.43, 8.97) * mm});
            skLineSegment(sketch, "E46.MirrorCS", {"start": v(-17.35, -20.96) * mm, "end": v(-19.8, -19.54) * mm});
            skLineSegment(sketch, "E47.MirrorCS", {"start": v(17.33, -20.96) * mm, "end": v(19.78, -19.54) * mm});
            skLineSegment(sketch, "E48.MirrorCS", {"start": v(10.42, -8.98) * mm, "end": v(12.87, -7.57) * mm});
            skLineSegment(sketch, "E49.MirrorCS", {"start": v(-10.43, -8.98) * mm, "end": v(-12.89, -7.57) * mm});
            skLineSegment(sketch, "E50.MirrorCS", {"start": v(10.42, -8.98) * mm, "end": v(17.33, -20.96) * mm});
            skLineSegment(sketch, "E51.MirrorCS", {"start": v(-19.8, -19.54) * mm, "end": v(-12.89, -7.57) * mm});
            skLineSegment(sketch, "E52.MirrorCS", {"start": v(-17.35, -20.96) * mm, "end": v(-10.43, -8.98) * mm});
            skLineSegment(sketch, "E53.MirrorCS", {"start": v(17.33, -20.96) * mm, "end": v(10.42, -8.98) * mm});
            skLineSegment(sketch, "E54.MirrorCS", {"start": v(19.78, -19.54) * mm, "end": v(12.87, -7.57) * mm});
            skSolve(sketch);
        }
        {
            var Q0;
            Q0=makeQuery(id+"F11.imprint","IMPRINT",FACE,{"disambiguationData":[TD([[makeQuery(id+"F11.imprint","IMPRINT",EDGE,{"derivedFrom":sQuery(id+"F11.wireOp",EDGE,"E42.MirrorCS")}),1.0]])]});
            var Q1;
            Q1=makeQuery(id+"F11.imprint","IMPRINT",FACE,{"disambiguationData":[TD([[makeQuery(id+"F11.imprint","IMPRINT",EDGE,{"derivedFrom":sQuery(id+"F11.wireOp",EDGE,"E46.MirrorCS")}),-1.0]])]});
            var Q2;
            Q2=makeQuery(id+"F11.imprint","IMPRINT",FACE,{"disambiguationData":[TD([[makeQuery(id+"F11.imprint","IMPRINT",EDGE,{"derivedFrom":sQuery(id+"F11.wireOp",EDGE,"E47.MirrorCS")}),1.0]])]});
            var Q3;
            Q3=makeQuery(id+"F11.imprint","IMPRINT",FACE,{"disambiguationData":[TD([[makeQuery(id+"F11.imprint","IMPRINT",EDGE,{"derivedFrom":sQuery(id+"F11.wireOp",EDGE,"E38")}),-1.0]])]});
            extrude(context, id + "F12", {"entities" : qUnion([Q0, Q1, Q2, Q3]), "operationType" : NewBodyOperationType.REMOVE, "oppositeDirection" : true, "depth" : 2.54 * mm, "offsetDistance" : 25.4 * mm});
        }
        {
            var Q0;
            Q0=makeQuery(id+"F12.boolean.opBoolean","COPY",EDGE,{"derivedFrom":makeQuery(id+"F12.opExtrude","CAP_EDGE",EDGE,{"disambiguationData":[OSD([sQuery(id+"F11.wireOp",EDGE,"E41.MirrorCS")])],"isStart":false})});
            var Q1;
            Q1=makeQuery(id+"F12.boolean.opBoolean","COPY",EDGE,{"derivedFrom":makeQuery(id+"F12.opExtrude","CAP_EDGE",EDGE,{"disambiguationData":[OSD([sQuery(id+"F11.wireOp",EDGE,"E40.MirrorCS")])],"isStart":false})});
            var Q2;
            Q2=makeQuery(id+"F12.boolean.opBoolean","COPY",EDGE,{"derivedFrom":makeQuery(id+"F12.opExtrude","CAP_EDGE",EDGE,{"disambiguationData":[OSD([sQuery(id+"F11.wireOp",EDGE,"E43.MirrorCS")])],"isStart":false})});
            var Q3;
            Q3=makeQuery(id+"F12.boolean.opBoolean","COPY",EDGE,{"derivedFrom":makeQuery(id+"F12.opExtrude","CAP_EDGE",EDGE,{"disambiguationData":[OSD([sQuery(id+"F11.wireOp",EDGE,"E51.MirrorCS")])],"isStart":false})});
            var Q4;
            Q4=makeQuery(id+"F12.boolean.opBoolean","COPY",EDGE,{"derivedFrom":makeQuery(id+"F12.opExtrude","CAP_EDGE",EDGE,{"disambiguationData":[OSD([sQuery(id+"F11.wireOp",EDGE,"E53.MirrorCS")])],"isStart":false})});
            var Q5;
            Q5=makeQuery(id+"F12.boolean.opBoolean","COPY",EDGE,{"derivedFrom":makeQuery(id+"F12.opExtrude","CAP_EDGE",EDGE,{"disambiguationData":[OSD([sQuery(id+"F11.wireOp",EDGE,"E45.MirrorCS")])],"isStart":false})});
            var Q6;
            Q6=makeQuery(id+"F12.boolean.opBoolean","COPY",EDGE,{"derivedFrom":makeQuery(id+"F12.opExtrude","CAP_EDGE",EDGE,{"disambiguationData":[OSD([sQuery(id+"F11.wireOp",EDGE,"E54.MirrorCS")])],"isStart":false})});
            var Q7;
            Q7=makeQuery(id+"F12.boolean.opBoolean","COPY",EDGE,{"derivedFrom":makeQuery(id+"F12.opExtrude","CAP_EDGE",EDGE,{"disambiguationData":[OSD([sQuery(id+"F11.wireOp",EDGE,"E52.MirrorCS")])],"isStart":false})});
            chamfer(context, id + "F13", {"entities" : qUnion([Q0, Q1, Q2, Q3, Q4, Q5, Q6, Q7]), "width" : 2.54 * mm, "tangentPropagation" : true});
        }
    });
